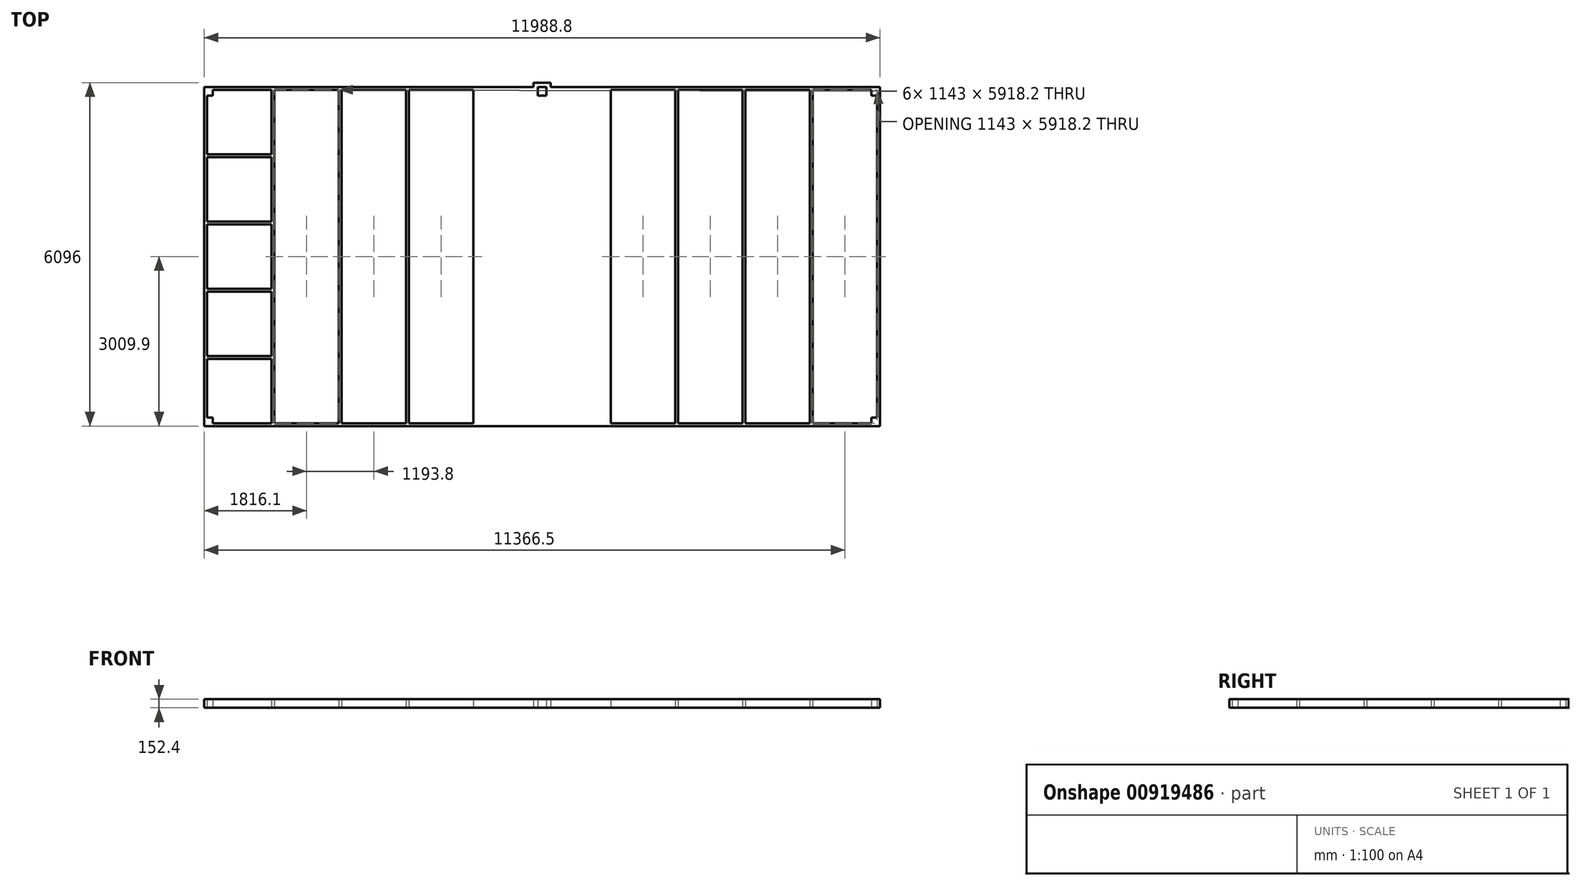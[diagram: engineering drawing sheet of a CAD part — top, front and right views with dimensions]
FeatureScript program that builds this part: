
annotation { "Feature Type Name" : "Feature", "Feature Type Description" : "" }
export const myFeature = defineFeature(function(context is Context, id is Id, definition is map)
    precondition{}
    {
        {
            var Q0;
            Q0=qCreatedBy(makeId("Top.planeOp"),FACE);
            var sketch = newSketch(context, id + "F0", { "sketchPlane" : qUnion([Q0])});
            skLineSegment(sketch, "E0.bottom", {"start": v(1141, 5379.5) * mm, "end": v(1191.8, 5379.5) * mm});
            skLineSegment(sketch, "E0.top", {"start": v(1141, -538.7) * mm, "end": v(1191.8, -538.7) * mm});
            skLineSegment(sketch, "E0.left", {"start": v(1141, 5379.5) * mm, "end": v(1141, -538.7) * mm});
            skLineSegment(sketch, "E0.right", {"start": v(1191.8, 5379.5) * mm, "end": v(1191.8, -538.7) * mm});
            skLineSegment(sketch, "E1.bottom", {"start": v(2334.8, 5379.5) * mm, "end": v(2385.6, 5379.5) * mm});
            skLineSegment(sketch, "E1.top", {"start": v(2334.8, -538.7) * mm, "end": v(2385.6, -538.7) * mm});
            skLineSegment(sketch, "E1.left", {"start": v(2334.8, 5379.5) * mm, "end": v(2334.8, -538.7) * mm});
            skLineSegment(sketch, "E1.right", {"start": v(2385.6, 5379.5) * mm, "end": v(2385.6, -538.7) * mm});
            skLineSegment(sketch, "E2.bottom", {"start": v(3528.6, 5379.5) * mm, "end": v(3579.4, 5379.5) * mm});
            skLineSegment(sketch, "E2.top", {"start": v(3528.6, -538.7) * mm, "end": v(3579.4, -538.7) * mm});
            skLineSegment(sketch, "E2.left", {"start": v(3528.6, 5379.5) * mm, "end": v(3528.6, -538.7) * mm});
            skLineSegment(sketch, "E2.right", {"start": v(3579.4, 5379.5) * mm, "end": v(3579.4, -538.7) * mm});
            skLineSegment(sketch, "E3.top", {"start": v(4722.4, -538.7) * mm, "end": v(4773.2, -538.7) * mm});
            skLineSegment(sketch, "E3.left", {"start": v(4722.4, 5277.9) * mm, "end": v(4722.4, -538.7) * mm});
            skLineSegment(sketch, "E3.right", {"start": v(4773.2, 5277.9) * mm, "end": v(4773.2, -538.7) * mm});
            skLineSegment(sketch, "E4.bottom", {"start": v(5916.2, 5379.5) * mm, "end": v(5967, 5379.5) * mm});
            skLineSegment(sketch, "E4.top", {"start": v(5916.2, -538.7) * mm, "end": v(5967, -538.7) * mm});
            skLineSegment(sketch, "E4.left", {"start": v(5916.2, 5379.5) * mm, "end": v(5916.2, -538.7) * mm});
            skLineSegment(sketch, "E4.right", {"start": v(5967, 5379.5) * mm, "end": v(5967, -538.7) * mm});
            skLineSegment(sketch, "E5.bottom", {"start": v(7110, 5379.5) * mm, "end": v(7160.8, 5379.5) * mm});
            skLineSegment(sketch, "E5.top", {"start": v(7110, -538.7) * mm, "end": v(7160.8, -538.7) * mm});
            skLineSegment(sketch, "E5.left", {"start": v(7110, 5379.5) * mm, "end": v(7110, -538.7) * mm});
            skLineSegment(sketch, "E5.right", {"start": v(7160.8, 5379.5) * mm, "end": v(7160.8, -538.7) * mm});
            skLineSegment(sketch, "E6.bottom", {"start": v(8303.8, 5379.5) * mm, "end": v(8354.6, 5379.5) * mm});
            skLineSegment(sketch, "E6.top", {"start": v(8303.8, -538.7) * mm, "end": v(8354.6, -538.7) * mm});
            skLineSegment(sketch, "E6.left", {"start": v(8303.8, 5379.5) * mm, "end": v(8303.8, -538.7) * mm});
            skLineSegment(sketch, "E6.right", {"start": v(8354.6, 5379.5) * mm, "end": v(8354.6, -538.7) * mm});
            skLineSegment(sketch, "E7.bottom", {"start": v(-52.8, 5379.5) * mm, "end": v(-2, 5379.5) * mm});
            skLineSegment(sketch, "E7.top", {"start": v(-52.8, -538.7) * mm, "end": v(-2, -538.7) * mm});
            skLineSegment(sketch, "E7.left", {"start": v(-52.8, 5379.5) * mm, "end": v(-52.8, -538.7) * mm});
            skLineSegment(sketch, "E7.right", {"start": v(-2, 5379.5) * mm, "end": v(-2, -538.7) * mm});
            skLineSegment(sketch, "E8.bottom", {"start": v(9497.6, 5379.5) * mm, "end": v(9548.4, 5379.5) * mm});
            skLineSegment(sketch, "E8.top", {"start": v(9497.6, -538.7) * mm, "end": v(9548.4, -538.7) * mm});
            skLineSegment(sketch, "E8.left", {"start": v(9497.6, 5379.5) * mm, "end": v(9497.6, -538.7) * mm});
            skLineSegment(sketch, "E8.right", {"start": v(9548.4, 5379.5) * mm, "end": v(9548.4, -538.7) * mm});
            skLineSegment(sketch, "E9.bottom", {"start": v(10691.4, 5277.9) * mm, "end": v(10742.2, 5277.9) * mm});
            skLineSegment(sketch, "E9.top", {"start": v(10691.4, -437.1) * mm, "end": v(10742.2, -437.1) * mm});
            skLineSegment(sketch, "E9.left", {"start": v(10691.4, 5277.9) * mm, "end": v(10691.4, -437.1) * mm});
            skLineSegment(sketch, "E9.right", {"start": v(10742.2, 5277.9) * mm, "end": v(10742.2, -437.1) * mm});
            skLineSegment(sketch, "E10.bottom", {"start": v(-1246.6, 5277.9) * mm, "end": v(-1195.8, 5277.9) * mm});
            skLineSegment(sketch, "E10.top", {"start": v(-1246.6, -437.1) * mm, "end": v(-1195.8, -437.1) * mm});
            skLineSegment(sketch, "E10.left", {"start": v(-1246.6, 5277.9) * mm, "end": v(-1246.6, -437.1) * mm});
            skLineSegment(sketch, "E10.right", {"start": v(-1195.8, 5277.9) * mm, "end": v(-1195.8, -437.1) * mm});
            skLineSegment(sketch, "E11.bottom", {"start": v(-1094.2, -538.7) * mm, "end": v(10589.8, -538.7) * mm});
            skLineSegment(sketch, "E11.top", {"start": v(-1094.2, -589.5) * mm, "end": v(10589.8, -589.5) * mm});
            skLineSegment(sketch, "E11.left", {"start": v(-1094.2, -538.7) * mm, "end": v(-1094.2, -589.5) * mm});
            skLineSegment(sketch, "E11.right", {"start": v(10589.8, -538.7) * mm, "end": v(10589.8, -589.5) * mm});
            skLineSegment(sketch, "E12.bottom", {"start": v(-1094.2, 5430.3) * mm, "end": v(10589.8, 5430.3) * mm});
            skLineSegment(sketch, "E12.top", {"start": v(-1094.2, 5379.5) * mm, "end": v(4671.6, 5379.5) * mm});
            skLineSegment(sketch, "E12.left", {"start": v(-1094.2, 5430.3) * mm, "end": v(-1094.2, 5379.5) * mm});
            skLineSegment(sketch, "E12.right", {"start": v(10589.8, 5430.3) * mm, "end": v(10589.8, 5379.5) * mm});
            skLineSegment(sketch, "E13.bottom", {"start": v(-1246.6, -437.1) * mm, "end": v(-1094.2, -437.1) * mm});
            skLineSegment(sketch, "E13.top", {"start": v(-1246.6, -589.5) * mm, "end": v(-1094.2, -589.5) * mm});
            skLineSegment(sketch, "E13.left", {"start": v(-1246.6, -437.1) * mm, "end": v(-1246.6, -589.5) * mm});
            skLineSegment(sketch, "E13.right", {"start": v(-1094.2, -437.1) * mm, "end": v(-1094.2, -589.5) * mm});
            skLineSegment(sketch, "E14.bottom", {"start": v(-1246.6, 5277.9) * mm, "end": v(-1094.2, 5277.9) * mm});
            skLineSegment(sketch, "E14.top", {"start": v(-1246.6, 5430.3) * mm, "end": v(-1094.2, 5430.3) * mm});
            skLineSegment(sketch, "E14.left", {"start": v(-1246.6, 5277.9) * mm, "end": v(-1246.6, 5430.3) * mm});
            skLineSegment(sketch, "E14.right", {"start": v(-1094.2, 5277.9) * mm, "end": v(-1094.2, 5430.3) * mm});
            skLineSegment(sketch, "E15.bottom", {"start": v(10742.2, -437.1) * mm, "end": v(10589.8, -437.1) * mm});
            skLineSegment(sketch, "E15.top", {"start": v(10742.2, -589.5) * mm, "end": v(10589.8, -589.5) * mm});
            skLineSegment(sketch, "E15.left", {"start": v(10742.2, -437.1) * mm, "end": v(10742.2, -589.5) * mm});
            skLineSegment(sketch, "E15.right", {"start": v(10589.8, -437.1) * mm, "end": v(10589.8, -589.5) * mm});
            skLineSegment(sketch, "E16.bottom", {"start": v(10742.2, 5277.9) * mm, "end": v(10589.8, 5277.9) * mm});
            skLineSegment(sketch, "E16.top", {"start": v(10742.2, 5430.3) * mm, "end": v(10589.8, 5430.3) * mm});
            skLineSegment(sketch, "E16.left", {"start": v(10742.2, 5277.9) * mm, "end": v(10742.2, 5430.3) * mm});
            skLineSegment(sketch, "E16.right", {"start": v(10589.8, 5277.9) * mm, "end": v(10589.8, 5430.3) * mm});
            skLineSegment(sketch, "E17.bottom", {"start": v(-1195.8, 655.1) * mm, "end": v(-52.8, 655.1) * mm});
            skLineSegment(sketch, "E17.top", {"start": v(-1195.8, 604.3) * mm, "end": v(-52.8, 604.3) * mm});
            skLineSegment(sketch, "E17.left", {"start": v(-1195.8, 655.1) * mm, "end": v(-1195.8, 604.3) * mm});
            skLineSegment(sketch, "E17.right", {"start": v(-52.8, 655.1) * mm, "end": v(-52.8, 604.3) * mm});
            skLineSegment(sketch, "E18.bottom", {"start": v(-1195.8, 4236.5) * mm, "end": v(-52.8, 4236.5) * mm});
            skLineSegment(sketch, "E18.top", {"start": v(-1195.8, 4185.7) * mm, "end": v(-52.8, 4185.7) * mm});
            skLineSegment(sketch, "E18.left", {"start": v(-1195.8, 4236.5) * mm, "end": v(-1195.8, 4185.7) * mm});
            skLineSegment(sketch, "E18.right", {"start": v(-52.8, 4236.5) * mm, "end": v(-52.8, 4185.7) * mm});
            skLineSegment(sketch, "E19.bottom", {"start": v(-1195.8, 3042.7) * mm, "end": v(-52.8, 3042.7) * mm});
            skLineSegment(sketch, "E19.top", {"start": v(-1195.8, 2991.9) * mm, "end": v(-52.8, 2991.9) * mm});
            skLineSegment(sketch, "E19.left", {"start": v(-1195.8, 3042.7) * mm, "end": v(-1195.8, 2991.9) * mm});
            skLineSegment(sketch, "E19.right", {"start": v(-52.8, 3042.7) * mm, "end": v(-52.8, 2991.9) * mm});
            skLineSegment(sketch, "E20.bottom", {"start": v(-1195.8, 1848.9) * mm, "end": v(-52.8, 1848.9) * mm});
            skLineSegment(sketch, "E20.top", {"start": v(-1195.8, 1798.1) * mm, "end": v(-52.8, 1798.1) * mm});
            skLineSegment(sketch, "E20.left", {"start": v(-1195.8, 1848.9) * mm, "end": v(-1195.8, 1798.1) * mm});
            skLineSegment(sketch, "E20.right", {"start": v(-52.8, 1848.9) * mm, "end": v(-52.8, 1798.1) * mm});
            skLineSegment(sketch, "E21.bottom", {"start": v(4671.6, 5430.3) * mm, "end": v(4824, 5430.3) * mm});
            skLineSegment(sketch, "E21.top", {"start": v(4671.6, 5277.9) * mm, "end": v(4824, 5277.9) * mm});
            skLineSegment(sketch, "E21.left", {"start": v(4671.6, 5430.3) * mm, "end": v(4671.6, 5277.9) * mm});
            skLineSegment(sketch, "E21.right", {"start": v(4824, 5430.3) * mm, "end": v(4824, 5277.9) * mm});
            skLineSegment(sketch, "E22.trimOffspring", {"start": v(4824, 5379.5) * mm, "end": v(10589.8, 5379.5) * mm});
            skLineSegment(sketch, "E23.bottom", {"start": v(4595.4, 5506.5) * mm, "end": v(4900.2, 5506.5) * mm});
            skLineSegment(sketch, "E23.top", {"start": v(4595.4, 5201.7) * mm, "end": v(4900.2, 5201.7) * mm});
            skLineSegment(sketch, "E23.left", {"start": v(4595.4, 5506.5) * mm, "end": v(4595.4, 5201.7) * mm});
            skLineSegment(sketch, "E23.right", {"start": v(4900.2, 5506.5) * mm, "end": v(4900.2, 5201.7) * mm});
            skSolve(sketch);
        }
        {
            var Q0;
            Q0 = qSketchRegion(id + "F0", true);
            var Q1;
            {var subQ0=sQuery(id+"F0.wireOp",EDGE,"E12.top");var subQ1=sQuery(id+"F0.wireOp",EDGE,"E3.left");var subQ2=makeQuery(id+"F0.imprint","INTERSECT",VERTEX,{"derivedFrom":[subQ1,subQ0]});Q1=makeQuery(id+"F0.imprint","IMPRINT",FACE,{"disambiguationData":[TD([[makeQuery(id+"F0.imprint","IMPRINT",EDGE,{"disambiguationData":[TD([[subQ2,-1.0]])],"derivedFrom":subQ1}),-1.0]])]});}
            var Q2;
            {var subQ0=sQuery(id+"F0.wireOp",EDGE,"E12.top");var subQ1=sQuery(id+"F0.wireOp",EDGE,"E3.left");var subQ2=makeQuery(id+"F0.imprint","INTERSECT",VERTEX,{"derivedFrom":[subQ1,subQ0]});Q2=makeQuery(id+"F0.imprint","IMPRINT",FACE,{"disambiguationData":[TD([[makeQuery(id+"F0.imprint","IMPRINT",EDGE,{"disambiguationData":[TD([[subQ2,-1.0]])],"derivedFrom":subQ1}),1.0]])]});}
            var Q3;
            {var subQ0=sQuery(id+"F0.wireOp",EDGE,"E12.top");var subQ1=sQuery(id+"F0.wireOp",EDGE,"E3.right");var subQ2=makeQuery(id+"F0.imprint","INTERSECT",VERTEX,{"derivedFrom":[subQ1,subQ0]});Q3=makeQuery(id+"F0.imprint","IMPRINT",FACE,{"disambiguationData":[TD([[makeQuery(id+"F0.imprint","IMPRINT",EDGE,{"disambiguationData":[TD([[subQ2,-1.0]])],"derivedFrom":subQ1}),1.0]])]});}
            var Q4;
            {var subQ0=sQuery(id+"F0.wireOp",EDGE,"E11.bottom");var subQ1=sQuery(id+"F0.wireOp",EDGE,"E3.left");var subQ2=makeQuery(id+"F0.imprint","INTERSECT",VERTEX,{"derivedFrom":[subQ1,subQ0]});Q4=makeQuery(id+"F0.imprint","IMPRINT",FACE,{"disambiguationData":[TD([[makeQuery(id+"F0.imprint","IMPRINT",EDGE,{"disambiguationData":[TD([[subQ2,1.0]])],"derivedFrom":subQ1}),1.0]])]});}
            var Q5;
            {var subQ0=sQuery(id+"F0.wireOp",EDGE,"E2.left");Q5=makeQuery(id+"F0.imprint","IMPRINT",FACE,{"disambiguationData":[TD([[makeQuery(id+"F0.imprint","IMPRINT",EDGE,{"derivedFrom":subQ0}),1.0]])]});}
            var Q6;
            {var subQ4=sQuery(id+"F0.wireOp",EDGE,"E7.right");Q6=makeQuery(id+"F0.imprint","IMPRINT",FACE,{"disambiguationData":[TD([[makeQuery(id+"F0.imprint","IMPRINT",EDGE,{"derivedFrom":subQ4}),-1.0]])]});}
            var Q7;
            Q7=makeQuery(id+"F0.imprint","IMPRINT",FACE,{"disambiguationData":[TD([[makeQuery(id+"F0.imprint","IMPRINT",EDGE,{"derivedFrom":sQuery(id+"F0.wireOp",EDGE,"E18.bottom")}),-1.0]])]});
            var Q8;
            {var subQ0=sQuery(id+"F0.wireOp",EDGE,"E0.left");Q8=makeQuery(id+"F0.imprint","IMPRINT",FACE,{"disambiguationData":[TD([[makeQuery(id+"F0.imprint","IMPRINT",EDGE,{"derivedFrom":subQ0}),1.0]])]});}
            var Q9;
            {var subQ0=sQuery(id+"F0.wireOp",EDGE,"E1.left");Q9=makeQuery(id+"F0.imprint","IMPRINT",FACE,{"disambiguationData":[TD([[makeQuery(id+"F0.imprint","IMPRINT",EDGE,{"derivedFrom":subQ0}),1.0]])]});}
            var Q10;
            Q10=makeQuery(id+"F0.imprint","IMPRINT",FACE,{"disambiguationData":[TD([[makeQuery(id+"F0.imprint","IMPRINT",EDGE,{"derivedFrom":sQuery(id+"F0.wireOp",EDGE,"E19.bottom")}),-1.0]])]});
            var Q11;
            Q11=makeQuery(id+"F0.imprint","IMPRINT",FACE,{"disambiguationData":[TD([[makeQuery(id+"F0.imprint","IMPRINT",EDGE,{"derivedFrom":sQuery(id+"F0.wireOp",EDGE,"E20.bottom")}),-1.0]])]});
            var Q12;
            Q12=makeQuery(id+"F0.imprint","IMPRINT",FACE,{"disambiguationData":[TD([[makeQuery(id+"F0.imprint","IMPRINT",EDGE,{"derivedFrom":sQuery(id+"F0.wireOp",EDGE,"E17.bottom")}),-1.0]])]});
            var Q13;
            {var subQ0=sQuery(id+"F0.wireOp",EDGE,"E4.left");Q13=makeQuery(id+"F0.imprint","IMPRINT",FACE,{"disambiguationData":[TD([[makeQuery(id+"F0.imprint","IMPRINT",EDGE,{"derivedFrom":subQ0}),1.0]])]});}
            var Q14;
            {var subQ0=sQuery(id+"F0.wireOp",EDGE,"E5.left");Q14=makeQuery(id+"F0.imprint","IMPRINT",FACE,{"disambiguationData":[TD([[makeQuery(id+"F0.imprint","IMPRINT",EDGE,{"derivedFrom":subQ0}),1.0]])]});}
            var Q15;
            {var subQ0=sQuery(id+"F0.wireOp",EDGE,"E6.left");Q15=makeQuery(id+"F0.imprint","IMPRINT",FACE,{"disambiguationData":[TD([[makeQuery(id+"F0.imprint","IMPRINT",EDGE,{"derivedFrom":subQ0}),1.0]])]});}
            var Q16;
            {var subQ0=sQuery(id+"F0.wireOp",EDGE,"E8.left");Q16=makeQuery(id+"F0.imprint","IMPRINT",FACE,{"disambiguationData":[TD([[makeQuery(id+"F0.imprint","IMPRINT",EDGE,{"derivedFrom":subQ0}),1.0]])]});}
            extrude(context, id + "F1", {"entities" : qUnion([Q0, Q1, Q2, Q3, Q4, Q5, Q6, Q7, Q8, Q9, Q10, Q11, Q12, Q13, Q14, Q15, Q16]), "depth" : 152.4 * mm, "offsetDistance" : 25 * mm});
        }
    });
